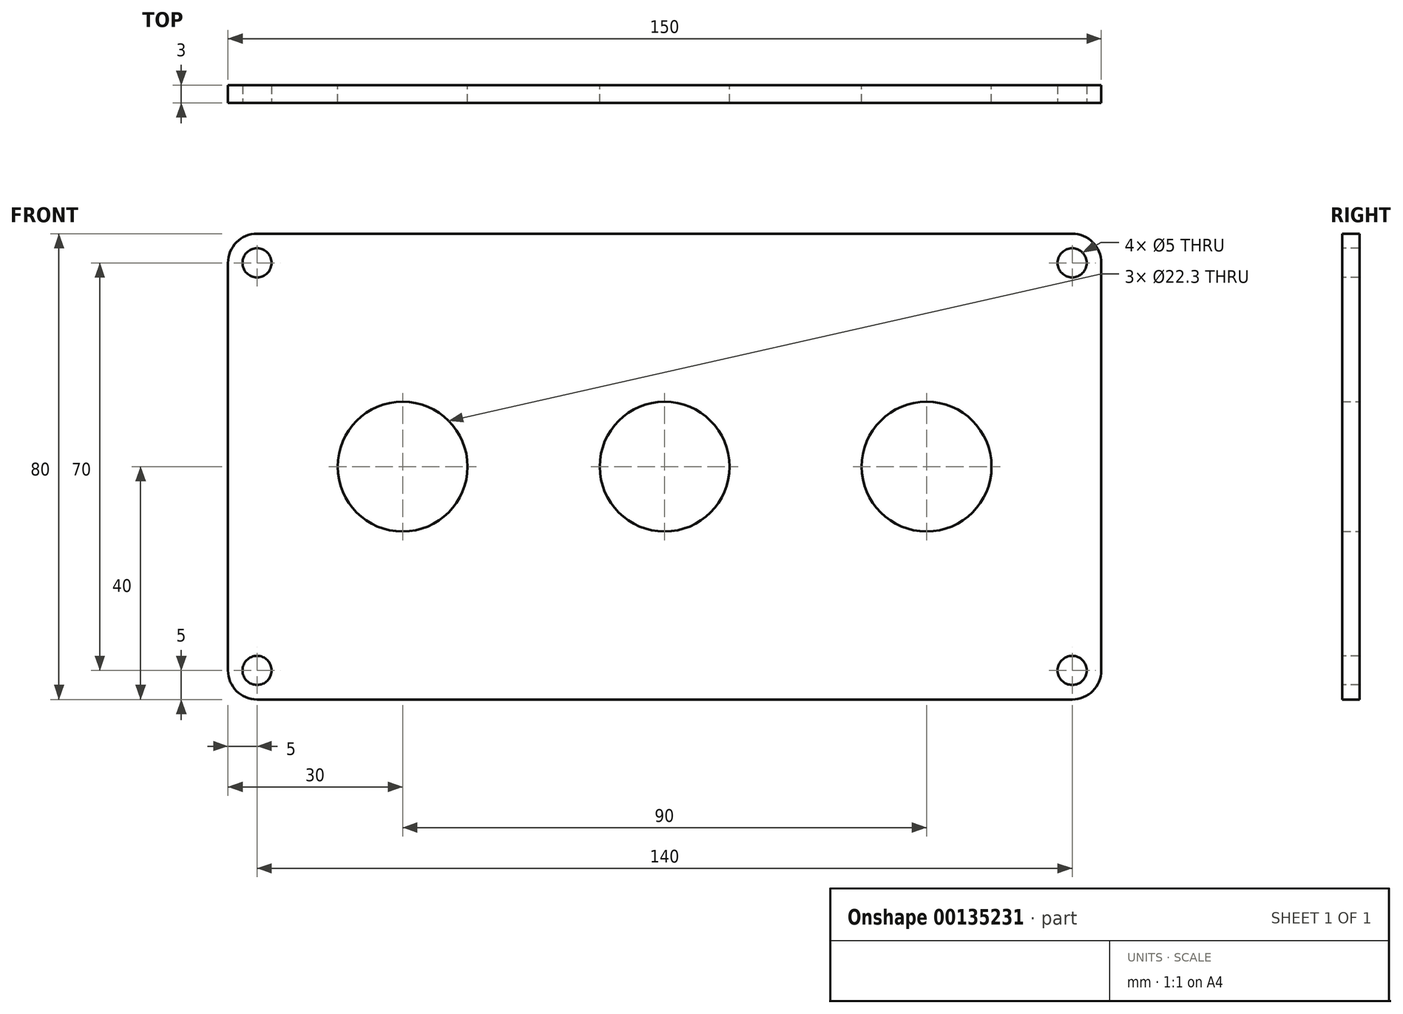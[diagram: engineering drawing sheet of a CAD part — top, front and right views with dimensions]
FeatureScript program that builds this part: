
annotation { "Feature Type Name" : "Feature", "Feature Type Description" : "" }
export const myFeature = defineFeature(function(context is Context, id is Id, definition is map)
    precondition{}
    {
        {
            var Q0;
            Q0=qCreatedBy(makeId("Front.planeOp"),FACE);
            var sketch = newSketch(context, id + "F0", { "sketchPlane" : qUnion([Q0])});
            skLineSegment(sketch, "E0.bottom", {"start": v(75, -40) * mm, "end": v(-75, -40) * mm});
            skLineSegment(sketch, "E0.top", {"start": v(75, 40) * mm, "end": v(-75, 40) * mm});
            skLineSegment(sketch, "E0.left", {"start": v(75, -40) * mm, "end": v(75, 40) * mm});
            skLineSegment(sketch, "E0.right", {"start": v(-75, -40) * mm, "end": v(-75, 40) * mm});
            skPoint(sketch, "E0.middle", {"position": v(0, 0) * mm});
            skCircle(sketch, "E1", {"center": v(-45, 0) * mm, "radius": 11.15 * mm});
            skCircle(sketch, "E2", {"center": v(0, 0) * mm, "radius": 11.15 * mm});
            skCircle(sketch, "E3", {"center": v(45, 0) * mm, "radius": 11.15 * mm});
            skSolve(sketch);
        }
        {
            var Q0;
            Q0=makeQuery(id+"F0.imprint","IMPRINT",FACE,{"disambiguationData":[TD([[makeQuery(id+"F0.imprint","IMPRINT",EDGE,{"derivedFrom":sQuery(id+"F0.wireOp",EDGE,"E0.bottom")}),-1.0]])]});
            extrude(context, id + "F1", {"entities" : qUnion([Q0]), "depth" : 3 * mm});
        }
        {
            var Q0;
            Q0=makeQuery(id+"F1.opExtrude","CAP_FACE",FACE,{"disambiguationData":[OSD([sQuery(id+"F0.wireOp",EDGE,"E0.bottom"),sQuery(id+"F0.wireOp",EDGE,"E0.top"),sQuery(id+"F0.wireOp",EDGE,"E0.left"),sQuery(id+"F0.wireOp",EDGE,"E0.right"),sQuery(id+"F0.wireOp",EDGE,"E1"),sQuery(id+"F0.wireOp",EDGE,"E2"),sQuery(id+"F0.wireOp",EDGE,"E3")])],"isStart":false});
            var sketch = newSketch(context, id + "F2", { "sketchPlane" : qUnion([Q0])});
            skCircle(sketch, "E4", {"center": v(-70, 35) * mm, "radius": 2.5 * mm});
            skCircle(sketch, "E5", {"center": v(70, 35) * mm, "radius": 2.5 * mm});
            skCircle(sketch, "E6", {"center": v(70, -35) * mm, "radius": 2.5 * mm});
            skCircle(sketch, "E7", {"center": v(-70, -35) * mm, "radius": 2.5 * mm});
            skSolve(sketch);
        }
        {
            var Q0;
            Q0 = qSketchRegion(id + "F2", true);
            extrude(context, id + "F3", {"entities" : qUnion([Q0]), "operationType" : NewBodyOperationType.REMOVE, "endBound" : BoundingType.UP_TO_NEXT, "oppositeDirection" : true, "depth" : 25 * mm});
        }
        {
            var Q0;
            Q0=makeQuery(id+"F1.opExtrude","SWEPT_EDGE",EDGE,{"disambiguationData":[OSD([sQuery(id+"F0.wireOp",EDGE,"E0.top"),sQuery(id+"F0.wireOp",EDGE,"E0.right")])]});
            var Q1;
            Q1=makeQuery(id+"F1.opExtrude","SWEPT_EDGE",EDGE,{"disambiguationData":[OSD([sQuery(id+"F0.wireOp",EDGE,"E0.top"),sQuery(id+"F0.wireOp",EDGE,"E0.left")])]});
            var Q2;
            Q2=makeQuery(id+"F1.opExtrude","SWEPT_EDGE",EDGE,{"disambiguationData":[OSD([sQuery(id+"F0.wireOp",EDGE,"E0.bottom"),sQuery(id+"F0.wireOp",EDGE,"E0.left")])]});
            var Q3;
            Q3=makeQuery(id+"F1.opExtrude","SWEPT_EDGE",EDGE,{"disambiguationData":[OSD([sQuery(id+"F0.wireOp",EDGE,"E0.bottom"),sQuery(id+"F0.wireOp",EDGE,"E0.right")])]});
            fillet(context, id + "F4", {"entities" : qUnion([Q0, Q1, Q2, Q3]), "radius" : 5 * mm, "tangentPropagation" : true, "allowEdgeOverflow" : false});
        }
    });
